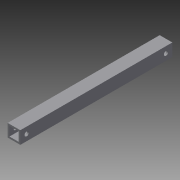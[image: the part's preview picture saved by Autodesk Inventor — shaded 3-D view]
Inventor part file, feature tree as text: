
AUTODESK INVENTOR PART (.ipt)
format: ipt  version: 2013 (Build 170138000, 138)  size: 103,424 bytes
history: native  units: in
note: dims shown in document units (in); Inventor stores cm internally (conversion verified against a paired STEP export)
features: extrude x2, sketch x2
ambient origin geometry x8: Origin, YZ Plane, XZ Plane, XY Plane, X Axis, Y Axis, Z Axis, Center Point
bodies: Solid1 (feature_tree)
feature tree (4):
  extrude  "Extrusion1"  Depth=0.5in
  extrude  "Extrusion2"  Depth=0.43in
  sketch  "Sketch1"  dims[d0=0.5in d1=0.5in]
  sketch  "Sketch2"  dims[d2=0.43in d3=0.43in d4=6.0in d5=0.0in d6=0.168in d7=0.25in d8=0.168in d9=0.25in d10=0.5in d11=0.0in]
